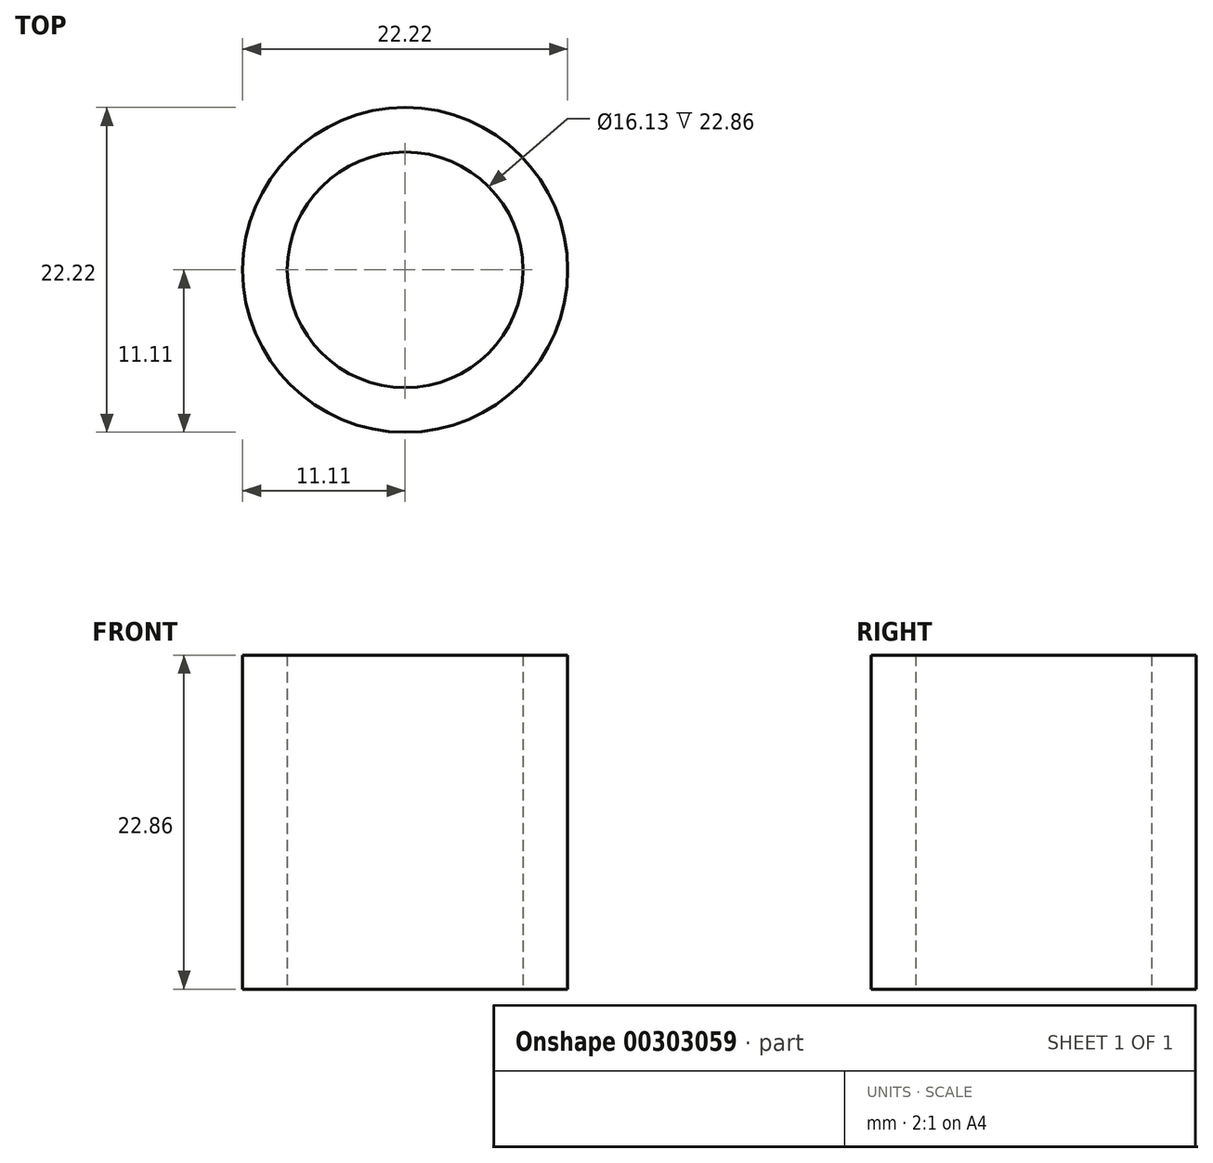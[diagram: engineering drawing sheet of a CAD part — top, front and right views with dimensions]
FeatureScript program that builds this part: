
annotation { "Feature Type Name" : "Feature", "Feature Type Description" : "" }
export const myFeature = defineFeature(function(context is Context, id is Id, definition is map)
    precondition{}
    {
        {
            var Q0;
            Q0=qCreatedBy(makeId("Top.planeOp"),FACE);
            var sketch = newSketch(context, id + "F0", { "sketchPlane" : qUnion([Q0])});
            skCircle(sketch, "E0", {"center": v(0, 0) * mm, "radius": 8.06 * mm});
            skCircle(sketch, "E1", {"center": v(0, 0) * mm, "radius": 11.11 * mm});
            skSolve(sketch);
        }
        {
            var Q0;
            Q0=makeQuery(id+"F0.imprint","IMPRINT",FACE,{"disambiguationData":[TD([[makeQuery(id+"F0.imprint","IMPRINT",EDGE,{"derivedFrom":sQuery(id+"F0.wireOp",EDGE,"E0")}),-1.0]])]});
            extrude(context, id + "F1", {"entities" : qUnion([Q0]), "depth" : 22.86 * mm, "symmetric" : true});
        }
    });
